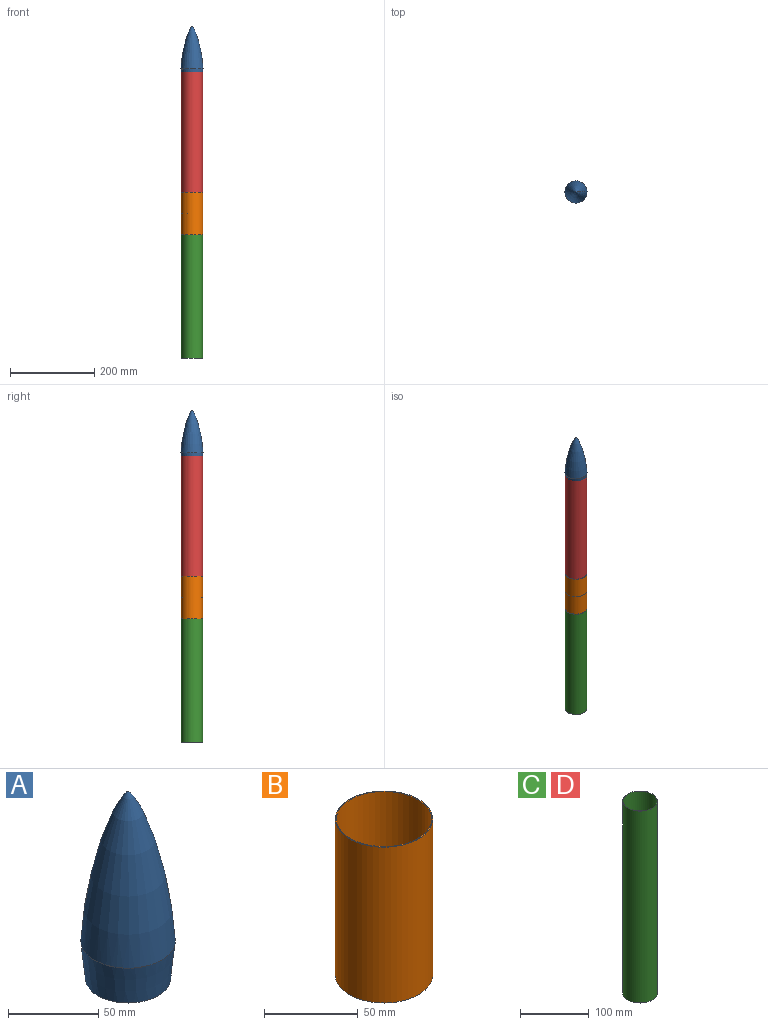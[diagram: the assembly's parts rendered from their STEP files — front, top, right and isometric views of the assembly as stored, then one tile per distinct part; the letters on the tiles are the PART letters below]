
ASSEMBLY  parts=4 mates=3
PART A: 7 faces, bbox 156x156x231 mm
  f0: cone r=23.62mm half-angle=5.7deg, axis (0,0,1), area 3992.4mm2, adj f1,f4
  f1: revolved ~101.92x52.32mm, area 11516.3mm2, adj f0
  f2: plane 50.74x50.74mm, normal (0,0,-1), area 2022.2mm2, adj f3
  f3: cone r=22.86mm half-angle=5.7deg, axis (0,0,1), area 3817.9mm2, adj f2,f4
  f4: cone r=22.86mm half-angle=84.3deg, axis (0,0,-1), area 111.3mm2, adj f0,f3
  f5: revolved ~51.82x25.91mm, area 0mm2, adj f6
  f6: plane 155.45x155.45mm, normal (0,0,1), area 2108.7mm2, adj f5
PART B: 4 faces, bbox 51.8x51.8x101.6 mm
  f0: cylinder r=25.4mm len=101.6mm, axis (0,0,-1), area 16214.6mm2, adj f2,f3
  f1: cylinder r=25.91mm len=101.6mm, axis (0,0,-1), area 16538.9mm2, adj f2,f3
  f2: plane 51.82x51.82mm, normal (0,0,1), area 81.9mm2, adj f0,f1
  f3: plane 51.82x51.82mm, normal (0,0,-1), area 81.9mm2, adj f0,f1
PART C: 4 faces, bbox 50.8x50.8x342.9 mm
  f0: cylinder r=24.89mm len=342.9mm, axis (0,0,-1), area 53629.9mm2, adj f2,f3
  f1: cylinder r=25.4mm len=342.9mm, axis (0,0,-1), area 54724.4mm2, adj f2,f3
  f2: plane 50.8x50.8mm, normal (0,0,1), area 80.3mm2, adj f0,f1
  f3: plane 50.8x50.8mm, normal (0,0,-1), area 80.3mm2, adj f0,f1
PART D: same geometry as C
PLACE A t=(0,0,686.05)mm
PLACE B t=(49.43,-42.49,292.1)mm
PLACE C at identity
PLACE D t=(0,0,342.9)mm
MATE fastened A.f0 <-> D.f0  axis (0,0,-1) through (0,0,685.8)mm
MATE cylindrical B.f0 <-> C.f0  axis (0,0,-1) through (0,0,342.9)mm
MATE cylindrical D.f0 <-> C.f0  axis (0,0,-1) through (0,0,342.9)mm
